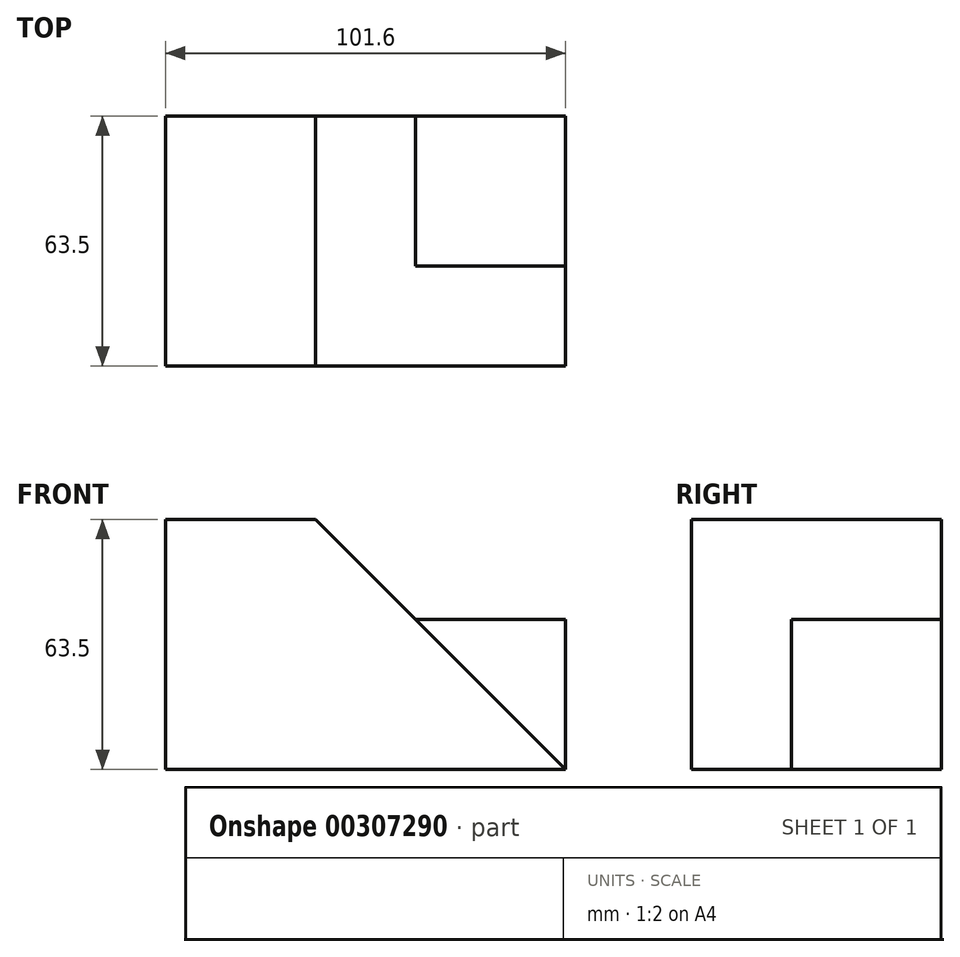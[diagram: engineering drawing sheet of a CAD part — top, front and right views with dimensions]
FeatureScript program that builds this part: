
annotation { "Feature Type Name" : "Feature", "Feature Type Description" : "" }
export const myFeature = defineFeature(function(context is Context, id is Id, definition is map)
    precondition{}
    {
        {
            var Q0;
            Q0=qCreatedBy(makeId("Front.planeOp"),FACE);
            var sketch = newSketch(context, id + "F0", { "sketchPlane" : qUnion([Q0])});
            skLineSegment(sketch, "E0", {"start": v(-48.86, -54.07) * mm, "end": v(52.74, -54.07) * mm});
            skLineSegment(sketch, "E1", {"start": v(-48.86, -54.07) * mm, "end": v(-48.86, 9.43) * mm});
            skLineSegment(sketch, "E2", {"start": v(-48.86, 9.43) * mm, "end": v(-10.76, 9.43) * mm});
            skLineSegment(sketch, "E3", {"start": v(-10.76, 9.43) * mm, "end": v(52.74, -54.07) * mm});
            skSolve(sketch);
        }
        {
            var Q0;
            Q0=makeQuery(id+"F0.imprint","IMPRINT",FACE,{"disambiguationData":[TD([[makeQuery(id+"F0.imprint","IMPRINT",EDGE,{"derivedFrom":sQuery(id+"F0.wireOp",EDGE,"E0")}),1.0]])]});
            extrude(context, id + "F1", {"entities" : qUnion([Q0]), "depth" : 63.5 * mm});
        }
        {
            var Q0;
            Q0=makeQuery(id+"F1.opExtrude","CAP_FACE",FACE,{"disambiguationData":[OSD([sQuery(id+"F0.wireOp",EDGE,"E0"),sQuery(id+"F0.wireOp",EDGE,"E1"),sQuery(id+"F0.wireOp",EDGE,"E2"),sQuery(id+"F0.wireOp",EDGE,"E3")])],"isStart":true});
            var sketch = newSketch(context, id + "F2", { "sketchPlane" : qUnion([Q0])});
            skLineSegment(sketch, "E4", {"start": v(-14.64, -15.97) * mm, "end": v(-52.74, -15.97) * mm});
            skLineSegment(sketch, "E5", {"start": v(-52.74, -15.97) * mm, "end": v(-52.74, -54.07) * mm});
            skSolve(sketch);
        }
        {
            var Q0;
            {var subQ0=sQuery(id+"F2.wireOp",EDGE,"E4");Q0=makeQuery(id+"F2.imprint","IMPRINT",FACE,{"disambiguationData":[TD([[makeQuery(id+"F2.imprint","IMPRINT",EDGE,{"derivedFrom":subQ0}),1.0]])]});}
            extrude(context, id + "F3", {"entities" : qUnion([Q0]), "operationType" : NewBodyOperationType.ADD, "oppositeDirection" : true, "depth" : 38.1 * mm});
        }
    });
